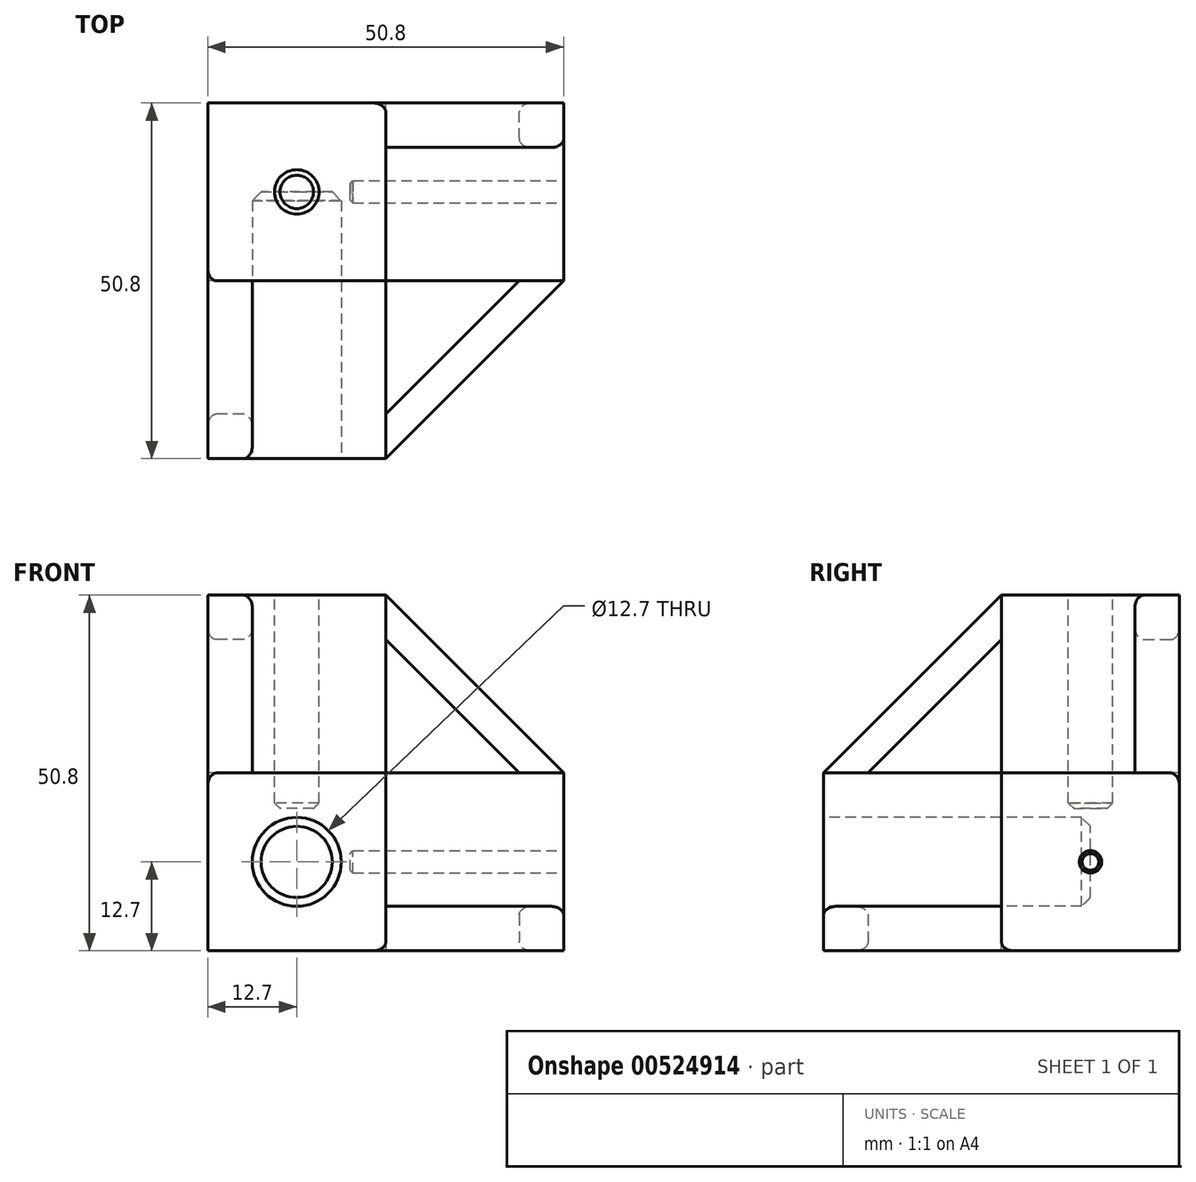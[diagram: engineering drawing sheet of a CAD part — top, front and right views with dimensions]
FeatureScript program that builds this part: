
annotation { "Feature Type Name" : "Feature", "Feature Type Description" : "" }
export const myFeature = defineFeature(function(context is Context, id is Id, definition is map)
    precondition{}
    {
        {
            var Q0;
            Q0=qCreatedBy(makeId("Top.planeOp"),FACE);
            var sketch = newSketch(context, id + "F0", { "sketchPlane" : qUnion([Q0])});
            skLineSegment(sketch, "E0.top", {"start": v(-12.7, 12.7) * mm, "end": v(12.7, 12.7) * mm});
            skLineSegment(sketch, "E0.left", {"start": v(-12.7, -12.7) * mm, "end": v(-12.7, 12.7) * mm});
            skLineSegment(sketch, "E0.right", {"start": v(12.7, -12.7) * mm, "end": v(12.7, 12.7) * mm});
            skLineSegment(sketch, "E1", {"start": v(-12.7, -12.7) * mm, "end": v(12.7, -12.7) * mm});
            skSolve(sketch);
        }
        {
            var Q0;
            Q0 = qSketchRegion(id + "F0", true);
            extrude(context, id + "F1", {"entities" : qUnion([Q0]), "depth" : 25.4 * mm, "offsetDistance" : 25.4 * mm, "symmetric" : true});
        }
        {
            var Q0;
            Q0=makeQuery(id+"F1.opExtrude","CAP_FACE",FACE,{"disambiguationData":[OSD([sQuery(id+"F0.wireOp",EDGE,"E0.top"),sQuery(id+"F0.wireOp",EDGE,"E0.left"),sQuery(id+"F0.wireOp",EDGE,"E0.right"),sQuery(id+"F0.wireOp",EDGE,"E1")])],"isStart":false});
            var sketch = newSketch(context, id + "F2", { "sketchPlane" : qUnion([Q0])});
            skCircle(sketch, "E2", {"center": v(0, 0) * mm, "radius": 3.17 * mm});
            skSolve(sketch);
        }
        {
            var Q0;
            Q0 = qSketchRegion(id + "F2", true);
            extrude(context, id + "F3", {"entities" : qUnion([Q0]), "operationType" : NewBodyOperationType.REMOVE, "oppositeDirection" : true, "depth" : 5.08 * mm, "offsetDistance" : 25.4 * mm});
        }
        {
            var Q0;
            Q0=makeQuery(id+"F1.opExtrude","SWEPT_FACE",FACE,{"disambiguationData":[OSD([sQuery(id+"F0.wireOp",EDGE,"E0.right")])]});
            var sketch = newSketch(context, id + "F4", { "sketchPlane" : qUnion([Q0])});
            skCircle(sketch, "E3", {"center": v(0, 0) * mm, "radius": 1.59 * mm});
            skSolve(sketch);
        }
        {
            var Q0;
            Q0 = qSketchRegion(id + "F4", true);
            extrude(context, id + "F5", {"entities" : qUnion([Q0]), "operationType" : NewBodyOperationType.REMOVE, "oppositeDirection" : true, "depth" : 5.08 * mm, "offsetDistance" : 25.4 * mm});
        }
        {
            var Q0;
            Q0=makeQuery(id+"F1.opExtrude","SWEPT_FACE",FACE,{"disambiguationData":[OSD([sQuery(id+"F0.wireOp",EDGE,"E1")])]});
            var sketch = newSketch(context, id + "F6", { "sketchPlane" : qUnion([Q0])});
            skCircle(sketch, "E4", {"center": v(0, 0) * mm, "radius": 6.35 * mm});
            skSolve(sketch);
        }
        {
            var Q0;
            Q0 = qSketchRegion(id + "F6", true);
            extrude(context, id + "F7", {"entities" : qUnion([Q0]), "operationType" : NewBodyOperationType.REMOVE, "oppositeDirection" : true, "depth" : 12.7 * mm, "offsetDistance" : 25.4 * mm});
        }
        {
            var Q0;
            Q0=makeQuery(id+"F7.boolean.opBoolean","COPY",EDGE,{"derivedFrom":makeQuery(id+"F7.opExtrude","CAP_EDGE",EDGE,{"disambiguationData":[OSD([sQuery(id+"F6.wireOp",EDGE,"E4")])],"isStart":false})});
            chamfer(context, id + "F8", {"entities" : qUnion([Q0]), "width" : 1.27 * mm, "tangentPropagation" : true});
        }
        {
            var Q0;
            Q0=makeQuery(id+"F5.boolean.opBoolean","COPY",EDGE,{"derivedFrom":makeQuery(id+"F5.opExtrude","CAP_EDGE",EDGE,{"disambiguationData":[OSD([sQuery(id+"F4.wireOp",EDGE,"E3")])],"isStart":false})});
            chamfer(context, id + "F9", {"entities" : qUnion([Q0]), "width" : 0.4 * mm, "tangentPropagation" : true});
        }
        {
            var Q0;
            Q0=makeQuery(id+"F3.boolean.opBoolean","COPY",EDGE,{"derivedFrom":makeQuery(id+"F3.opExtrude","CAP_EDGE",EDGE,{"disambiguationData":[OSD([sQuery(id+"F2.wireOp",EDGE,"E2")])],"isStart":false})});
            chamfer(context, id + "F10", {"entities" : qUnion([Q0]), "width" : 0.8 * mm, "tangentPropagation" : true});
        }
        {
            var Q0;
            Q0=makeQuery(id+"F1.opExtrude","SWEPT_FACE",FACE,{"disambiguationData":[OSD([sQuery(id+"F0.wireOp",EDGE,"E0.right")])]});
            var sketch = newSketch(context, id + "F11", { "sketchPlane" : qUnion([Q0])});
            skLineSegment(sketch, "E5.bottom", {"start": v(-12.7, -12.7) * mm, "end": v(12.7, -12.7) * mm});
            skLineSegment(sketch, "E5.top", {"start": v(-12.7, 12.7) * mm, "end": v(12.7, 12.7) * mm});
            skLineSegment(sketch, "E5.left", {"start": v(-12.7, -12.7) * mm, "end": v(-12.7, 12.7) * mm});
            skLineSegment(sketch, "E5.right", {"start": v(12.7, -12.7) * mm, "end": v(12.7, 12.7) * mm});
            skCircle(sketch, "E6", {"center": v(0, 0) * mm, "radius": 1.59 * mm});
            skSolve(sketch);
        }
        {
            var Q0;
            Q0 = qSketchRegion(id + "F11", true);
            extrude(context, id + "F12", {"entities" : qUnion([Q0]), "operationType" : NewBodyOperationType.ADD, "depth" : 25.4 * mm, "offsetDistance" : 25.4 * mm});
        }
        {
            var Q0;
            Q0=makeQuery(id+"F12.boolean.opBoolean","MERGE",FACE,{"derivedFrom":[makeQuery(id+"F1.opExtrude","SWEPT_FACE",FACE,{"disambiguationData":[OSD([sQuery(id+"F0.wireOp",EDGE,"E1")])]}),makeQuery(id+"F12.opExtrude","SWEPT_FACE",FACE,{"disambiguationData":[OSD([sQuery(id+"F11.wireOp",EDGE,"E5.left")])]})]});
            var sketch = newSketch(context, id + "F13", { "sketchPlane" : qUnion([Q0])});
            skLineSegment(sketch, "E7.bottom", {"start": v(-12.7, -12.7) * mm, "end": v(12.7, -12.7) * mm});
            skLineSegment(sketch, "E7.top", {"start": v(-12.7, 12.7) * mm, "end": v(12.7, 12.7) * mm});
            skLineSegment(sketch, "E7.left", {"start": v(-12.7, -12.7) * mm, "end": v(-12.7, 12.7) * mm});
            skLineSegment(sketch, "E7.right", {"start": v(12.7, -12.7) * mm, "end": v(12.7, 12.7) * mm});
            skCircle(sketch, "E8", {"center": v(0, 0) * mm, "radius": 6.35 * mm});
            skSolve(sketch);
        }
        {
            var Q0;
            Q0 = qSketchRegion(id + "F13", true);
            extrude(context, id + "F14", {"entities" : qUnion([Q0]), "operationType" : NewBodyOperationType.ADD, "depth" : 25.4 * mm, "offsetDistance" : 25.4 * mm});
        }
        {
            var Q0;
            Q0=makeQuery(id+"F14.boolean.opBoolean","MERGE",FACE,{"derivedFrom":[makeQuery(id+"F12.boolean.opBoolean","MERGE",FACE,{"derivedFrom":[makeQuery(id+"F1.opExtrude","CAP_FACE",FACE,{"disambiguationData":[OSD([sQuery(id+"F0.wireOp",EDGE,"E0.top"),sQuery(id+"F0.wireOp",EDGE,"E0.left"),sQuery(id+"F0.wireOp",EDGE,"E0.right"),sQuery(id+"F0.wireOp",EDGE,"E1")])],"isStart":false}),makeQuery(id+"F12.opExtrude","SWEPT_FACE",FACE,{"disambiguationData":[OSD([sQuery(id+"F11.wireOp",EDGE,"E5.top")])]})]}),makeQuery(id+"F14.opExtrude","SWEPT_FACE",FACE,{"disambiguationData":[OSD([sQuery(id+"F13.wireOp",EDGE,"E7.top")])]})]});
            var sketch = newSketch(context, id + "F15", { "sketchPlane" : qUnion([Q0])});
            skLineSegment(sketch, "E9.bottom", {"start": v(-12.7, 12.7) * mm, "end": v(12.7, 12.7) * mm});
            skLineSegment(sketch, "E9.top", {"start": v(-12.7, -12.7) * mm, "end": v(12.7, -12.7) * mm});
            skLineSegment(sketch, "E9.left", {"start": v(-12.7, 12.7) * mm, "end": v(-12.7, -12.7) * mm});
            skLineSegment(sketch, "E9.right", {"start": v(12.7, 12.7) * mm, "end": v(12.7, -12.7) * mm});
            skCircle(sketch, "E10", {"center": v(0, 0) * mm, "radius": 3.18 * mm});
            skSolve(sketch);
        }
        {
            var Q0;
            Q0 = qSketchRegion(id + "F15", true);
            extrude(context, id + "F16", {"entities" : qUnion([Q0]), "operationType" : NewBodyOperationType.ADD, "depth" : 25.4 * mm, "offsetDistance" : 25.4 * mm});
        }
        {
            var Q0;
            Q0=makeQuery(id+"F14.boolean.opBoolean","MERGE",FACE,{"derivedFrom":[makeQuery(id+"F12.boolean.opBoolean","MERGE",FACE,{"derivedFrom":[makeQuery(id+"F1.opExtrude","CAP_FACE",FACE,{"disambiguationData":[OSD([sQuery(id+"F0.wireOp",EDGE,"E0.top"),sQuery(id+"F0.wireOp",EDGE,"E0.left"),sQuery(id+"F0.wireOp",EDGE,"E0.right"),sQuery(id+"F0.wireOp",EDGE,"E1")])],"isStart":true}),makeQuery(id+"F12.opExtrude","SWEPT_FACE",FACE,{"disambiguationData":[OSD([sQuery(id+"F11.wireOp",EDGE,"E5.bottom")])]})]}),makeQuery(id+"F14.opExtrude","SWEPT_FACE",FACE,{"disambiguationData":[OSD([sQuery(id+"F13.wireOp",EDGE,"E7.bottom")])]})]});
            var sketch = newSketch(context, id + "F17", { "sketchPlane" : qUnion([Q0])});
            skLineSegment(sketch, "E11", {"start": v(12.7, 38.1) * mm, "end": v(38.1, 12.7) * mm});
            skLineSegment(sketch, "E12", {"start": v(38.1, 12.7) * mm, "end": v(31.75, 12.7) * mm});
            skLineSegment(sketch, "E13", {"start": v(31.75, 12.7) * mm, "end": v(12.7, 31.75) * mm});
            skLineSegment(sketch, "E14", {"start": v(12.7, 31.75) * mm, "end": v(12.7, 38.1) * mm});
            skSolve(sketch);
        }
        {
            var Q0;
            Q0 = qSketchRegion(id + "F17", true);
            extrude(context, id + "F18", {"entities" : qUnion([Q0]), "operationType" : NewBodyOperationType.ADD, "oppositeDirection" : true, "depth" : 6.35 * mm, "offsetDistance" : 25.4 * mm});
        }
        {
            var Q0;
            Q0=makeQuery(id+"F16.boolean.opBoolean","MERGE",FACE,{"derivedFrom":[makeQuery(id+"F12.boolean.opBoolean","MERGE",FACE,{"derivedFrom":[makeQuery(id+"F1.opExtrude","SWEPT_FACE",FACE,{"disambiguationData":[OSD([sQuery(id+"F0.wireOp",EDGE,"E0.top")])]}),makeQuery(id+"F12.opExtrude","SWEPT_FACE",FACE,{"disambiguationData":[OSD([sQuery(id+"F11.wireOp",EDGE,"E5.right")])]})]}),makeQuery(id+"F16.opExtrude","SWEPT_FACE",FACE,{"disambiguationData":[OSD([sQuery(id+"F15.wireOp",EDGE,"E9.bottom")])]})]});
            var sketch = newSketch(context, id + "F19", { "sketchPlane" : qUnion([Q0])});
            skLineSegment(sketch, "E15", {"start": v(-38.1, 12.7) * mm, "end": v(-12.7, 38.1) * mm});
            skLineSegment(sketch, "E16", {"start": v(-12.7, 38.1) * mm, "end": v(-12.7, 31.75) * mm});
            skLineSegment(sketch, "E17", {"start": v(-12.7, 31.75) * mm, "end": v(-31.75, 12.7) * mm});
            skLineSegment(sketch, "E18", {"start": v(-31.75, 12.7) * mm, "end": v(-38.1, 12.7) * mm});
            skSolve(sketch);
        }
        {
            var Q0;
            Q0 = qSketchRegion(id + "F19", true);
            extrude(context, id + "F20", {"entities" : qUnion([Q0]), "operationType" : NewBodyOperationType.ADD, "oppositeDirection" : true, "depth" : 6.35 * mm, "offsetDistance" : 25.4 * mm});
        }
        {
            var Q0;
            Q0=makeQuery(id+"F16.boolean.opBoolean","MERGE",FACE,{"derivedFrom":[makeQuery(id+"F14.boolean.opBoolean","MERGE",FACE,{"derivedFrom":[makeQuery(id+"F1.opExtrude","SWEPT_FACE",FACE,{"disambiguationData":[OSD([sQuery(id+"F0.wireOp",EDGE,"E0.left")])]}),makeQuery(id+"F14.opExtrude","SWEPT_FACE",FACE,{"disambiguationData":[OSD([sQuery(id+"F13.wireOp",EDGE,"E7.left")])]})]}),makeQuery(id+"F16.opExtrude","SWEPT_FACE",FACE,{"disambiguationData":[OSD([sQuery(id+"F15.wireOp",EDGE,"E9.left")])]})]});
            var sketch = newSketch(context, id + "F21", { "sketchPlane" : qUnion([Q0])});
            skLineSegment(sketch, "E19", {"start": v(12.7, 38.1) * mm, "end": v(38.1, 12.7) * mm});
            skLineSegment(sketch, "E20", {"start": v(38.1, 12.7) * mm, "end": v(31.75, 12.7) * mm});
            skLineSegment(sketch, "E21", {"start": v(31.75, 12.7) * mm, "end": v(12.7, 31.75) * mm});
            skLineSegment(sketch, "E22", {"start": v(12.7, 31.75) * mm, "end": v(12.7, 38.1) * mm});
            skSolve(sketch);
        }
        {
            var Q0;
            Q0 = qSketchRegion(id + "F21", true);
            extrude(context, id + "F22", {"entities" : qUnion([Q0]), "operationType" : NewBodyOperationType.ADD, "oppositeDirection" : true, "depth" : 6.35 * mm, "offsetDistance" : 25.4 * mm});
        }
        {
            var Q0;
            Q0=makeQuery(id+"F20.opExtrude","CAP_EDGE",EDGE,{"disambiguationData":[OSD([sQuery(id+"F19.wireOp",EDGE,"E15")])],"isStart":false});
            var Q1;
            Q1=makeQuery(id+"F20.opExtrude","CAP_EDGE",EDGE,{"disambiguationData":[OSD([sQuery(id+"F19.wireOp",EDGE,"E15")])],"isStart":true});
            var Q2;
            Q2=makeQuery(id+"F20.opExtrude","CAP_EDGE",EDGE,{"disambiguationData":[OSD([sQuery(id+"F19.wireOp",EDGE,"E17")])],"isStart":true});
            var Q3;
            Q3=makeQuery(id+"F20.opExtrude","CAP_EDGE",EDGE,{"disambiguationData":[OSD([sQuery(id+"F19.wireOp",EDGE,"E17")])],"isStart":false});
            var Q4;
            Q4=makeQuery(id+"F22.opExtrude","CAP_EDGE",EDGE,{"disambiguationData":[OSD([sQuery(id+"F21.wireOp",EDGE,"E19")])],"isStart":false});
            var Q5;
            Q5=makeQuery(id+"F22.opExtrude","CAP_EDGE",EDGE,{"disambiguationData":[OSD([sQuery(id+"F21.wireOp",EDGE,"E21")])],"isStart":false});
            var Q6;
            Q6=makeQuery(id+"F22.opExtrude","CAP_EDGE",EDGE,{"disambiguationData":[OSD([sQuery(id+"F21.wireOp",EDGE,"E19")])],"isStart":true});
            var Q7;
            Q7=makeQuery(id+"F22.opExtrude","CAP_EDGE",EDGE,{"disambiguationData":[OSD([sQuery(id+"F21.wireOp",EDGE,"E21")])],"isStart":true});
            var Q8;
            Q8=makeQuery(id+"F18.opExtrude","CAP_EDGE",EDGE,{"disambiguationData":[OSD([sQuery(id+"F17.wireOp",EDGE,"E11")])],"isStart":false});
            var Q9;
            Q9=makeQuery(id+"F18.opExtrude","CAP_EDGE",EDGE,{"disambiguationData":[OSD([sQuery(id+"F17.wireOp",EDGE,"E11")])],"isStart":true});
            var Q10;
            Q10=makeQuery(id+"F18.opExtrude","CAP_EDGE",EDGE,{"disambiguationData":[OSD([sQuery(id+"F17.wireOp",EDGE,"E13")])],"isStart":true});
            var Q11;
            Q11=makeQuery(id+"F18.opExtrude","CAP_EDGE",EDGE,{"disambiguationData":[OSD([sQuery(id+"F17.wireOp",EDGE,"E13")])],"isStart":false});
            fillet(context, id + "F23", {"entities" : qUnion([Q0, Q1, Q2, Q3, Q4, Q5, Q6, Q7, Q8, Q9, Q10, Q11]), "radius" : 1.27 * mm, "tangentPropagation" : true, "allowEdgeOverflow" : false});
        }
    });
